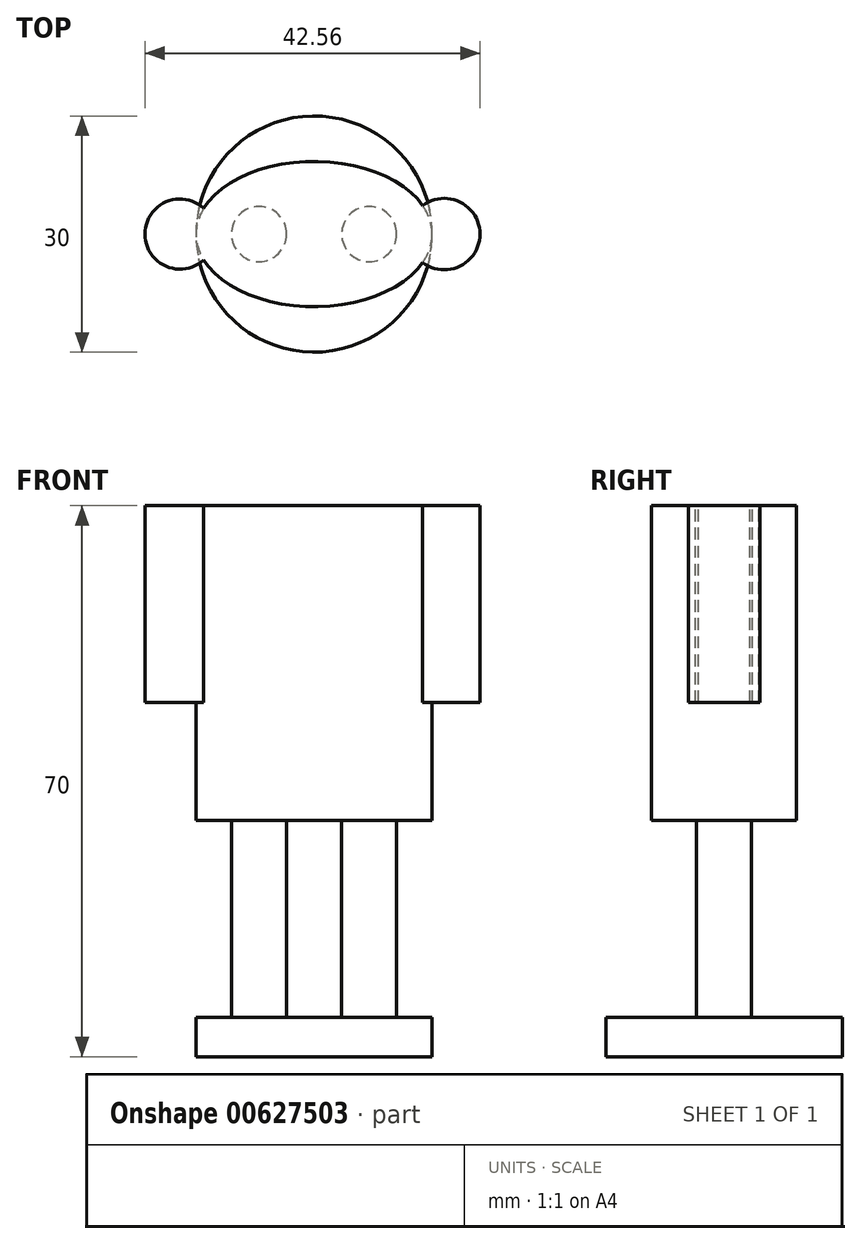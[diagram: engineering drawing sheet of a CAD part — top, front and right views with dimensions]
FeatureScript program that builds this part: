
annotation { "Feature Type Name" : "Feature", "Feature Type Description" : "" }
export const myFeature = defineFeature(function(context is Context, id is Id, definition is map)
    precondition{}
    {
        {
            var Q0;
            Q0=qCreatedBy(makeId("Top.planeOp"),FACE);
            var sketch = newSketch(context, id + "F0", { "sketchPlane" : qUnion([Q0])});
            skCircle(sketch, "E0", {"center": v(0, 0) * mm, "radius": 15 * mm});
            skSolve(sketch);
        }
        {
            var Q0;
            Q0=makeQuery(id+"F0.imprint","IMPRINT",FACE,{"disambiguationData":[TD([[makeQuery(id+"F0.imprint","IMPRINT",EDGE,{"derivedFrom":sQuery(id+"F0.wireOp",EDGE,"E0")}),1.0]])]});
            extrude(context, id + "F1", {"entities" : qUnion([Q0]), "depth" : 5 * mm, "offsetDistance" : 25 * mm});
        }
        {
            var Q0;
            Q0=makeQuery(id+"F1.opExtrude","CAP_FACE",FACE,{"disambiguationData":[OSD([sQuery(id+"F0.wireOp",EDGE,"E0")])],"isStart":false});
            var sketch = newSketch(context, id + "F2", { "sketchPlane" : qUnion([Q0])});
            skCircle(sketch, "E1", {"center": v(7, 0) * mm, "radius": 3.5 * mm});
            skCircle(sketch, "E2", {"center": v(-7, 0) * mm, "radius": 3.5 * mm});
            skSolve(sketch);
        }
        {
            var Q0;
            Q0 = qSketchRegion(id + "F2", true);
            extrude(context, id + "F3", {"entities" : qUnion([Q0]), "operationType" : NewBodyOperationType.ADD, "depth" : 25 * mm, "offsetDistance" : 25 * mm});
        }
        {
            var Q0;
            Q0=makeQuery(id+"F3.opExtrude","CAP_FACE",FACE,{"disambiguationData":[OSD([sQuery(id+"F2.wireOp",EDGE,"E2")])],"isStart":false});
            var sketch = newSketch(context, id + "F4", { "sketchPlane" : qUnion([Q0])});
            skEllipse(sketch, "E3", {"center": v(0, 0) * mm, "majorRadius": 15 * mm, "minorRadius": 9.22 * mm, "majorAxis": v(1, 0)});
            skSolve(sketch);
        }
        {
            var Q0;
            Q0 = qSketchRegion(id + "F4", true);
            extrude(context, id + "F5", {"entities" : qUnion([Q0]), "operationType" : NewBodyOperationType.ADD, "depth" : 40 * mm, "offsetDistance" : 25 * mm});
        }
        {
            var Q0;
            Q0=makeQuery(id+"F5.opExtrude","CAP_FACE",FACE,{"disambiguationData":[OSD([sQuery(id+"F4.wireOp",EDGE,"E3")])],"isStart":false});
            var sketch = newSketch(context, id + "F6", { "sketchPlane" : qUnion([Q0])});
            skCircle(sketch, "E4", {"center": v(16.53, 0) * mm, "radius": 4.54 * mm});
            skCircle(sketch, "E5", {"center": v(-17.03, 0) * mm, "radius": 4.46 * mm});
            skSolve(sketch);
        }
        {
            var Q0;
            {var subQ0=sQuery(id+"F6.wireOp",EDGE,"E5");var subQ1=makeQuery(id+"F5.opExtrude","CAP_EDGE",EDGE,{"disambiguationData":[OSD([sQuery(id+"F4.wireOp",EDGE,"E3")])],"isStart":false});var subQ2=makeQuery(id+"F6.imprint","INTERSECT",VERTEX,{"disambiguationData":[OD(0.0)],"derivedFrom":[subQ1,subQ0]});Q0=makeQuery(id+"F6.imprint","IMPRINT",FACE,{"disambiguationData":[TD([[makeQuery(id+"F6.imprint","IMPRINT",EDGE,{"disambiguationData":[TD([[subQ2,1.0]])],"derivedFrom":subQ0}),1.0]])]});}
            var Q1;
            {var subQ0=sQuery(id+"F6.wireOp",EDGE,"E4");var subQ1=makeQuery(id+"F5.opExtrude","CAP_EDGE",EDGE,{"disambiguationData":[OSD([sQuery(id+"F4.wireOp",EDGE,"E3")])],"isStart":false});var subQ2=makeQuery(id+"F6.imprint","INTERSECT",VERTEX,{"disambiguationData":[OD(0.0)],"derivedFrom":[subQ1,subQ0]});Q1=makeQuery(id+"F6.imprint","IMPRINT",FACE,{"disambiguationData":[TD([[makeQuery(id+"F6.imprint","IMPRINT",EDGE,{"disambiguationData":[TD([[subQ2,-1.0]])],"derivedFrom":subQ0}),1.0]])]});}
            extrude(context, id + "F7", {"entities" : qUnion([Q0, Q1]), "operationType" : NewBodyOperationType.ADD, "depth" : -25 * mm, "offsetDistance" : 25 * mm});
        }
    });
